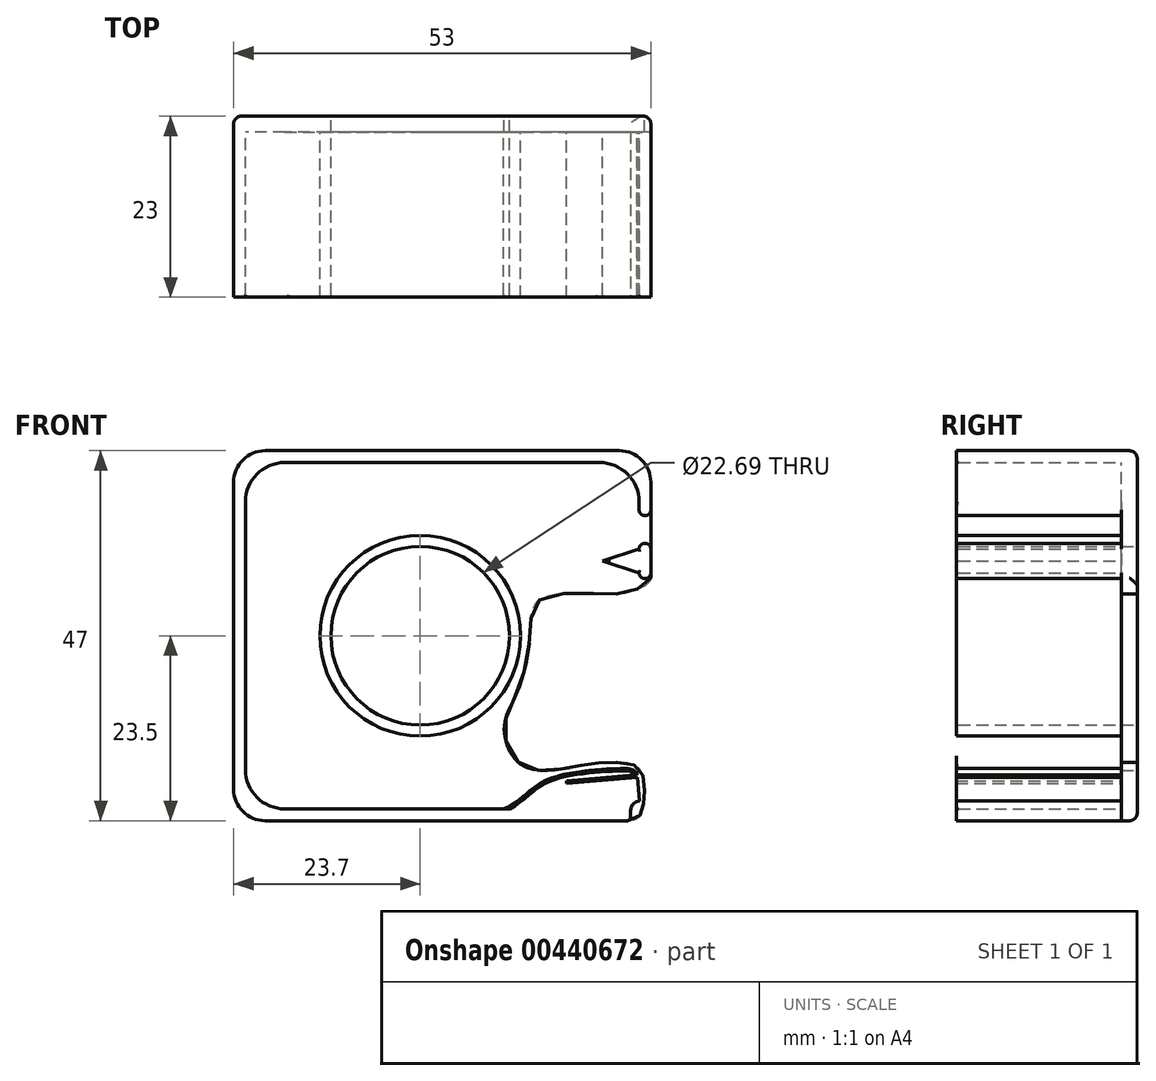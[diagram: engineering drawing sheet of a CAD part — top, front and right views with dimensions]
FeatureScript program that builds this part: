
annotation { "Feature Type Name" : "Feature", "Feature Type Description" : "" }
export const myFeature = defineFeature(function(context is Context, id is Id, definition is map)
    precondition{}
    {
        {
            var Q0;
            Q0=qCreatedBy(makeId("Front.planeOp"),FACE);
            var sketch = newSketch(context, id + "F0", { "sketchPlane" : qUnion([Q0])});
            skLineSegment(sketch, "E0.top", {"start": v(0, 47) * mm, "end": v(53, 47) * mm});
            skLineSegment(sketch, "E0.left", {"start": v(0, 0) * mm, "end": v(0, 47) * mm});
            skCircle(sketch, "E1", {"center": v(23.7, 23.5) * mm, "radius": 12.75 * mm});
            skCircle(sketch, "E2", {"center": v(23.7, 23.5) * mm, "radius": 11.35 * mm});
            skLineSegment(sketch, "E3", {"start": v(50, 0) * mm, "end": v(0, 0) * mm});
            skLineSegment(sketch, "E4", {"start": v(50, 1.5) * mm, "end": v(50, 0) * mm});
            skLineSegment(sketch, "E5", {"start": v(50, 1.5) * mm, "end": v(6.5, 1.5) * mm});
            skLineSegment(sketch, "E6", {"start": v(1.5, 6.5) * mm, "end": v(1.5, 40.5) * mm});
            skLineSegment(sketch, "E7", {"start": v(6.5, 45.5) * mm, "end": v(46.5, 45.5) * mm});
            skLineSegment(sketch, "E8", {"start": v(53, 47) * mm, "end": v(53, 39.5) * mm});
            skLineSegment(sketch, "E9", {"start": v(53, 47) * mm, "end": v(53, 0) * mm});
            skLineSegment(sketch, "E10", {"start": v(51.27, 5.5) * mm, "end": v(51.53, 2.51) * mm});
            skLineSegment(sketch, "E11", {"start": v(51.27, 5.5) * mm, "end": v(42.3, 4.72) * mm});
            skLineSegment(sketch, "E12", {"start": v(42.27, 5.06) * mm, "end": v(51.24, 5.85) * mm});
            skLineSegment(sketch, "E13", {"start": v(51.27, 5.5) * mm, "end": v(51.24, 5.85) * mm});
            skLineSegment(sketch, "E14", {"start": v(53, 0) * mm, "end": v(50, 0) * mm});
            skPoint(sketch, "E15.visualSharp", {"position": v(1.5, 45.5) * mm});
            skArc(sketch, "E15.filletArc", {"start": v(6.5, 45.5) * mm, "mid": v(2.96, 44.04) * mm, "end": v(1.5, 40.5) * mm});
            skPoint(sketch, "E16.visualSharp", {"position": v(1.5, 1.5) * mm});
            skArc(sketch, "E16.filletArc", {"start": v(1.5, 6.5) * mm, "mid": v(2.96, 2.96) * mm, "end": v(6.5, 1.5) * mm});
            skLineSegment(sketch, "E17", {"start": v(51.5, 40.5) * mm, "end": v(51.5, 39.5) * mm});
            skArc(sketch, "E18", {"start": v(51.5, 39.5) * mm, "mid": v(52.25, 38.75) * mm, "end": v(53, 39.5) * mm});
            skPoint(sketch, "E19.visualSharp", {"position": v(51.5, 45.5) * mm});
            skArc(sketch, "E19.filletArc", {"start": v(51.5, 40.5) * mm, "mid": v(50.04, 44.04) * mm, "end": v(46.5, 45.5) * mm});
            skLineSegment(sketch, "E20", {"start": v(42.27, 5.06) * mm, "end": v(42.3, 4.72) * mm});
            skFitSpline(sketch, "E21", {"points": [v(51.53, 2.51) * mm, v(50, 0) * mm], "startDerivative": vector(-5.77, -1.22) * mm, "endDerivative": vector(-2.95, 0) * mm});
            skLineSegment(sketch, "E22", {"start": v(51.5, 34.5) * mm, "end": v(51.5, 31.5) * mm});
            skLineSegment(sketch, "E23", {"start": v(51.5, 31.5) * mm, "end": v(53, 31.5) * mm});
            skLineSegment(sketch, "E24", {"start": v(53, 31.5) * mm, "end": v(53, 34.5) * mm});
            skLineSegment(sketch, "E25", {"start": v(53, 34.5) * mm, "end": v(51.5, 34.5) * mm});
            skArc(sketch, "E26", {"start": v(53, 34.5) * mm, "mid": v(52.25, 35.25) * mm, "end": v(51.5, 34.5) * mm});
            skArc(sketch, "E27", {"start": v(51.5, 31.5) * mm, "mid": v(52.25, 30.75) * mm, "end": v(53, 31.5) * mm});
            skLineSegment(sketch, "E28", {"start": v(51.5, 34.5) * mm, "end": v(46.88, 33) * mm});
            skLineSegment(sketch, "E29", {"start": v(46.88, 33) * mm, "end": v(51.5, 31.5) * mm});
            skFitSpline(sketch, "E30", {"points": [v(50, 0) * mm, v(51.6, 0.66) * mm, v(52.06, 1.98) * mm, v(52.18, 3.48) * mm, v(51.96, 5.77) * mm, v(50.85, 7.08) * mm, v(47.78, 7.4) * mm, v(44.94, 7.14) * mm, v(41.25, 6.53) * mm, v(36.65, 7.04) * mm, v(34.35, 11.65) * mm, v(36.09, 16.51) * mm, v(37.63, 23.35) * mm, v(38.73, 27.96) * mm, v(45.56, 28.87) * mm, v(50.24, 29.06) * mm, v(53, 30.86) * mm], "startDerivative": vector(67.36, 0) * mm, "endDerivative": vector(0, 38.99) * mm});
            skFitSpline(sketch, "E31", {"points": [v(51.24, 5.85) * mm, v(48.53, 6.62) * mm, v(43.83, 6.2) * mm, v(39.58, 5.1) * mm, v(36.96, 3.21) * mm, v(34.3, 1.5) * mm], "startDerivative": vector(-2.28, 14.98) * mm, "endDerivative": vector(-9.83, -1.8) * mm});
            skSolve(sketch);
        }
        {
            var Q0;
            Q0=makeQuery(id+"F0.imprint","IMPRINT",FACE,{"disambiguationData":[TD([[makeQuery(id+"F0.imprint","IMPRINT",EDGE,{"derivedFrom":sQuery(id+"F0.wireOp",EDGE,"E1")}),-1.0]])]});
            var Q1;
            Q1=makeQuery(id+"F0.imprint","IMPRINT",FACE,{"disambiguationData":[TD([[makeQuery(id+"F0.imprint","IMPRINT",EDGE,{"derivedFrom":sQuery(id+"F0.wireOp",EDGE,"E1")}),1.0]])]});
            var Q2;
            Q2=makeQuery(id+"F0.imprint","IMPRINT",FACE,{"disambiguationData":[TD([[makeQuery(id+"F0.imprint","IMPRINT",EDGE,{"derivedFrom":sQuery(id+"F0.wireOp",EDGE,"E0.top")}),-1.0]])]});
            var Q3;
            {var subQ0=sQuery(id+"F0.wireOp",EDGE,"E12");Q3=makeQuery(id+"F0.imprint","IMPRINT",FACE,{"disambiguationData":[TD([[makeQuery(id+"F0.imprint","IMPRINT",EDGE,{"derivedFrom":subQ0}),1.0]])]});}
            var Q4;
            {var subQ0=sQuery(id+"F0.wireOp",EDGE,"E11");Q4=makeQuery(id+"F0.imprint","IMPRINT",FACE,{"disambiguationData":[TD([[makeQuery(id+"F0.imprint","IMPRINT",EDGE,{"derivedFrom":subQ0}),-1.0]])]});}
            var Q5;
            {var subQ1=sQuery(id+"F0.wireOp",EDGE,"E4");Q5=makeQuery(id+"F0.imprint","IMPRINT",FACE,{"disambiguationData":[TD([[makeQuery(id+"F0.imprint","IMPRINT",EDGE,{"derivedFrom":subQ1}),1.0]])]});}
            var Q6;
            Q6=makeQuery(id+"F0.imprint","IMPRINT",FACE,{"disambiguationData":[TD([[makeQuery(id+"F0.imprint","IMPRINT",EDGE,{"derivedFrom":sQuery(id+"F0.wireOp",EDGE,"E22")}),1.0]])]});
            var Q7;
            Q7=makeQuery(id+"F0.imprint","IMPRINT",FACE,{"disambiguationData":[TD([[makeQuery(id+"F0.imprint","IMPRINT",EDGE,{"derivedFrom":sQuery(id+"F0.wireOp",EDGE,"E22")}),-1.0]])]});
            var Q8;
            Q8=makeQuery(id+"F0.imprint","IMPRINT",FACE,{"disambiguationData":[TD([[makeQuery(id+"F0.imprint","IMPRINT",EDGE,{"derivedFrom":sQuery(id+"F0.wireOp",EDGE,"E25")}),-1.0]])]});
            var Q9;
            Q9=makeQuery(id+"F0.imprint","IMPRINT",FACE,{"disambiguationData":[TD([[makeQuery(id+"F0.imprint","IMPRINT",EDGE,{"derivedFrom":sQuery(id+"F0.wireOp",EDGE,"E23")}),-1.0]])]});
            extrude(context, id + "F1", {"entities" : qUnion([Q0, Q1, Q2, Q3, Q4, Q5, Q6, Q7, Q8, Q9]), "depth" : 2 * mm});
        }
        {
            var Q0;
            Q0=makeQuery(id+"F0.imprint","IMPRINT",FACE,{"disambiguationData":[TD([[makeQuery(id+"F0.imprint","IMPRINT",EDGE,{"derivedFrom":sQuery(id+"F0.wireOp",EDGE,"E0.top")}),-1.0]])]});
            var Q1;
            Q1=makeQuery(id+"F0.imprint","IMPRINT",FACE,{"disambiguationData":[TD([[makeQuery(id+"F0.imprint","IMPRINT",EDGE,{"derivedFrom":sQuery(id+"F0.wireOp",EDGE,"E1")}),1.0]])]});
            var Q2;
            {var subQ0=sQuery(id+"F0.wireOp",EDGE,"E12");Q2=makeQuery(id+"F0.imprint","IMPRINT",FACE,{"disambiguationData":[TD([[makeQuery(id+"F0.imprint","IMPRINT",EDGE,{"derivedFrom":subQ0}),1.0]])]});}
            var Q3;
            {var subQ1=sQuery(id+"F0.wireOp",EDGE,"E4");Q3=makeQuery(id+"F0.imprint","IMPRINT",FACE,{"disambiguationData":[TD([[makeQuery(id+"F0.imprint","IMPRINT",EDGE,{"derivedFrom":subQ1}),1.0]])]});}
            var Q4;
            Q4=makeQuery(id+"F0.imprint","IMPRINT",FACE,{"disambiguationData":[TD([[makeQuery(id+"F0.imprint","IMPRINT",EDGE,{"derivedFrom":sQuery(id+"F0.wireOp",EDGE,"E22")}),1.0]])]});
            var Q5;
            Q5=makeQuery(id+"F0.imprint","IMPRINT",FACE,{"disambiguationData":[TD([[makeQuery(id+"F0.imprint","IMPRINT",EDGE,{"derivedFrom":sQuery(id+"F0.wireOp",EDGE,"E25")}),-1.0]])]});
            var Q6;
            Q6=makeQuery(id+"F0.imprint","IMPRINT",FACE,{"disambiguationData":[TD([[makeQuery(id+"F0.imprint","IMPRINT",EDGE,{"derivedFrom":sQuery(id+"F0.wireOp",EDGE,"E23")}),-1.0]])]});
            var Q7;
            Q7=makeQuery(id+"F0.imprint","IMPRINT",FACE,{"disambiguationData":[TD([[makeQuery(id+"F0.imprint","IMPRINT",EDGE,{"derivedFrom":sQuery(id+"F0.wireOp",EDGE,"E22")}),-1.0]])]});
            extrude(context, id + "F2", {"entities" : qUnion([Q0, Q1, Q2, Q3, Q4, Q5, Q6, Q7]), "operationType" : NewBodyOperationType.ADD, "depth" : 23 * mm});
        }
        {
            var Q0;
            {var subQ0=sQuery(id+"F0.wireOp",EDGE,"LASfMnGV-BYrx-Q03O-p0P8-yl39unLi5r6t");var subQ1=sQuery(id+"F0.wireOp",EDGE,"E0.top");Q0=makeQuery(id+"F2.boolean.opBoolean","MERGE",EDGE,{"derivedFrom":[makeQuery(id+"F1.opExtrude","SWEPT_EDGE",EDGE,{"disambiguationData":[OSD([subQ1,subQ0])]}),makeQuery(id+"F2.opExtrude","SWEPT_EDGE",EDGE,{"disambiguationData":[OSD([subQ1,subQ0])]})]});}
            var Q1;
            {var subQ0=sQuery(id+"F0.wireOp",EDGE,"E0.left");var subQ1=sQuery(id+"F0.wireOp",EDGE,"E0.top");Q1=makeQuery(id+"F2.boolean.opBoolean","MERGE",EDGE,{"derivedFrom":[makeQuery(id+"F1.opExtrude","SWEPT_EDGE",EDGE,{"disambiguationData":[OSD([subQ1,subQ0])]}),makeQuery(id+"F2.opExtrude","SWEPT_EDGE",EDGE,{"disambiguationData":[OSD([subQ1,subQ0])]})]});}
            var Q2;
            {var subQ0=sQuery(id+"F0.wireOp",EDGE,"E3");var subQ1=sQuery(id+"F0.wireOp",EDGE,"E0.left");Q2=makeQuery(id+"F2.boolean.opBoolean","MERGE",EDGE,{"derivedFrom":[makeQuery(id+"F1.opExtrude","SWEPT_EDGE",EDGE,{"disambiguationData":[OSD([subQ1,subQ0])]}),makeQuery(id+"F2.opExtrude","SWEPT_EDGE",EDGE,{"disambiguationData":[OSD([subQ1,subQ0])]})]});}
            fillet(context, id + "F3", {"entities" : qUnion([Q0, Q1, Q2]), "radius" : 4 * mm, "allowEdgeOverflow" : false});
        }
        {
            var Q0;
            Q0=makeQuery(id+"F1.opExtrude","CAP_EDGE",EDGE,{"disambiguationData":[OSD([sQuery(id+"F0.wireOp",EDGE,"E0.top")])],"isStart":true});
            var Q1;
            Q1=makeQuery(id+"F1.opExtrude","CAP_EDGE",EDGE,{"disambiguationData":[OSD([sQuery(id+"F0.wireOp",EDGE,"E0.left")])],"isStart":true});
            var Q2;
            Q2=makeQuery(id+"F1.opExtrude","CAP_EDGE",EDGE,{"disambiguationData":[OSD([sQuery(id+"F0.wireOp",EDGE,"E3")])],"isStart":true});
            var Q3;
            Q3=makeQuery(id+"F1.opExtrude","CAP_EDGE",EDGE,{"disambiguationData":[OSD([sQuery(id+"F0.wireOp",EDGE,"LASfMnGV-BYrx-Q03O-p0P8-yl39unLi5r6t"),sQuery(id+"F0.wireOp",EDGE,"E9")])],"isStart":true});
            var Q4;
            {var subQ0=sQuery(id+"F0.wireOp",EDGE,"E0.left");var subQ1=sQuery(id+"F0.wireOp",EDGE,"E0.top");Q4=makeQuery(id+"F3.opFillet","BLEND_EDGE",EDGE,{"blendedFrom":[makeQuery(id+"F2.boolean.opBoolean","MERGE",EDGE,{"derivedFrom":[makeQuery(id+"F1.opExtrude","SWEPT_EDGE",EDGE,{"disambiguationData":[OSD([subQ1,subQ0])]}),makeQuery(id+"F2.opExtrude","SWEPT_EDGE",EDGE,{"disambiguationData":[OSD([subQ1,subQ0])]})]}),makeQuery(id+"F1.opExtrude","CAP_FACE",FACE,{"disambiguationData":[OSD([subQ1,subQ0,sQuery(id+"F0.wireOp",EDGE,"E2"),sQuery(id+"F0.wireOp",EDGE,"E3"),sQuery(id+"F0.wireOp",EDGE,"E9"),sQuery(id+"F0.wireOp",EDGE,"E10"),sQuery(id+"F0.wireOp",EDGE,"E13"),sQuery(id+"F0.wireOp",EDGE,"96ae6e86-44be-4938-9890-4f7ba03de8a1"),sQuery(id+"F0.wireOp",EDGE,"2b4ca562-6351-4470-98a5-20ef774f2d19")])],"isStart":true})],"blendedInto":[makeQuery(id+"F1.opExtrude","CAP_FACE",FACE,{"disambiguationData":[OSD([subQ1,subQ0,sQuery(id+"F0.wireOp",EDGE,"E2"),sQuery(id+"F0.wireOp",EDGE,"E3"),sQuery(id+"F0.wireOp",EDGE,"E9"),sQuery(id+"F0.wireOp",EDGE,"E10"),sQuery(id+"F0.wireOp",EDGE,"E13"),sQuery(id+"F0.wireOp",EDGE,"96ae6e86-44be-4938-9890-4f7ba03de8a1"),sQuery(id+"F0.wireOp",EDGE,"2b4ca562-6351-4470-98a5-20ef774f2d19")])],"isStart":true})]});}
            var Q5;
            {var subQ0=sQuery(id+"F0.wireOp",EDGE,"E3");var subQ1=sQuery(id+"F0.wireOp",EDGE,"E0.left");Q5=makeQuery(id+"F3.opFillet","BLEND_EDGE",EDGE,{"blendedFrom":[makeQuery(id+"F2.boolean.opBoolean","MERGE",EDGE,{"derivedFrom":[makeQuery(id+"F1.opExtrude","SWEPT_EDGE",EDGE,{"disambiguationData":[OSD([subQ1,subQ0])]}),makeQuery(id+"F2.opExtrude","SWEPT_EDGE",EDGE,{"disambiguationData":[OSD([subQ1,subQ0])]})]}),makeQuery(id+"F1.opExtrude","CAP_FACE",FACE,{"disambiguationData":[OSD([sQuery(id+"F0.wireOp",EDGE,"E0.top"),subQ1,sQuery(id+"F0.wireOp",EDGE,"E2"),subQ0,sQuery(id+"F0.wireOp",EDGE,"E9"),sQuery(id+"F0.wireOp",EDGE,"E10"),sQuery(id+"F0.wireOp",EDGE,"E13"),sQuery(id+"F0.wireOp",EDGE,"96ae6e86-44be-4938-9890-4f7ba03de8a1"),sQuery(id+"F0.wireOp",EDGE,"2b4ca562-6351-4470-98a5-20ef774f2d19")])],"isStart":true})],"blendedInto":[makeQuery(id+"F1.opExtrude","CAP_FACE",FACE,{"disambiguationData":[OSD([sQuery(id+"F0.wireOp",EDGE,"E0.top"),subQ1,sQuery(id+"F0.wireOp",EDGE,"E2"),subQ0,sQuery(id+"F0.wireOp",EDGE,"E9"),sQuery(id+"F0.wireOp",EDGE,"E10"),sQuery(id+"F0.wireOp",EDGE,"E13"),sQuery(id+"F0.wireOp",EDGE,"96ae6e86-44be-4938-9890-4f7ba03de8a1"),sQuery(id+"F0.wireOp",EDGE,"2b4ca562-6351-4470-98a5-20ef774f2d19")])],"isStart":true})]});}
            var Q6;
            {var subQ0=sQuery(id+"F0.wireOp",EDGE,"E9");var subQ1=sQuery(id+"F0.wireOp",EDGE,"E0.top");Q6=makeQuery(id+"F3.opFillet","BLEND_EDGE",EDGE,{"blendedFrom":[makeQuery(id+"F2.boolean.opBoolean","MERGE",EDGE,{"derivedFrom":[makeQuery(id+"F1.opExtrude","SWEPT_EDGE",EDGE,{"disambiguationData":[OSD([subQ1,subQ0])]}),makeQuery(id+"F2.opExtrude","SWEPT_EDGE",EDGE,{"disambiguationData":[OSD([subQ1,subQ0])]})]}),makeQuery(id+"F1.opExtrude","CAP_FACE",FACE,{"disambiguationData":[OSD([subQ1,sQuery(id+"F0.wireOp",EDGE,"E0.left"),sQuery(id+"F0.wireOp",EDGE,"E2"),sQuery(id+"F0.wireOp",EDGE,"E3"),subQ0,sQuery(id+"F0.wireOp",EDGE,"E10"),sQuery(id+"F0.wireOp",EDGE,"E13"),sQuery(id+"F0.wireOp",EDGE,"96ae6e86-44be-4938-9890-4f7ba03de8a1"),sQuery(id+"F0.wireOp",EDGE,"2b4ca562-6351-4470-98a5-20ef774f2d19")])],"isStart":true})],"blendedInto":[makeQuery(id+"F1.opExtrude","CAP_FACE",FACE,{"disambiguationData":[OSD([subQ1,sQuery(id+"F0.wireOp",EDGE,"E0.left"),sQuery(id+"F0.wireOp",EDGE,"E2"),sQuery(id+"F0.wireOp",EDGE,"E3"),subQ0,sQuery(id+"F0.wireOp",EDGE,"E10"),sQuery(id+"F0.wireOp",EDGE,"E13"),sQuery(id+"F0.wireOp",EDGE,"96ae6e86-44be-4938-9890-4f7ba03de8a1"),sQuery(id+"F0.wireOp",EDGE,"2b4ca562-6351-4470-98a5-20ef774f2d19")])],"isStart":true})]});}
            fillet(context, id + "F4", {"entities" : qUnion([Q0, Q1, Q2, Q3, Q4, Q5, Q6]), "radius" : 1 * mm, "allowEdgeOverflow" : false});
        }
        {
            var Q0;
            Q0=makeQuery(id+"F2.opExtrude","CAP_EDGE",EDGE,{"disambiguationData":[OSD([sQuery(id+"F0.wireOp",EDGE,"E2")])],"isStart":false});
            var Q1;
            Q1=makeQuery(id+"F2.opExtrude","CAP_EDGE",EDGE,{"disambiguationData":[OSD([sQuery(id+"F0.wireOp",EDGE,"E15.filletArc")])],"isStart":false});
            var Q2;
            Q2=makeQuery(id+"F2.opExtrude","CAP_EDGE",EDGE,{"disambiguationData":[OSD([sQuery(id+"F0.wireOp",EDGE,"E16.filletArc")])],"isStart":false});
            var Q3;
            Q3=makeQuery(id+"F2.opExtrude","CAP_EDGE",EDGE,{"disambiguationData":[OSD([sQuery(id+"F0.wireOp",EDGE,"E19.filletArc")])],"isStart":false});
            var Q4;
            Q4=makeQuery(id+"F2.opExtrude","CAP_EDGE",EDGE,{"disambiguationData":[OSD([sQuery(id+"F0.wireOp",EDGE,"E28")])],"isStart":false});
            var Q5;
            Q5=makeQuery(id+"F2.opExtrude","CAP_EDGE",EDGE,{"disambiguationData":[OSD([sQuery(id+"F0.wireOp",EDGE,"E29")])],"isStart":false});
            var Q6;
            Q6=makeQuery(id+"F2.opExtrude","CAP_EDGE",EDGE,{"disambiguationData":[OSD([sQuery(id+"F0.wireOp",EDGE,"E31")])],"isStart":false});
            fillet(context, id + "F5", {"entities" : qUnion([Q0, Q1, Q2, Q3, Q4, Q5, Q6]), "radius" : 0.3 * mm, "allowEdgeOverflow" : false});
        }
    });
